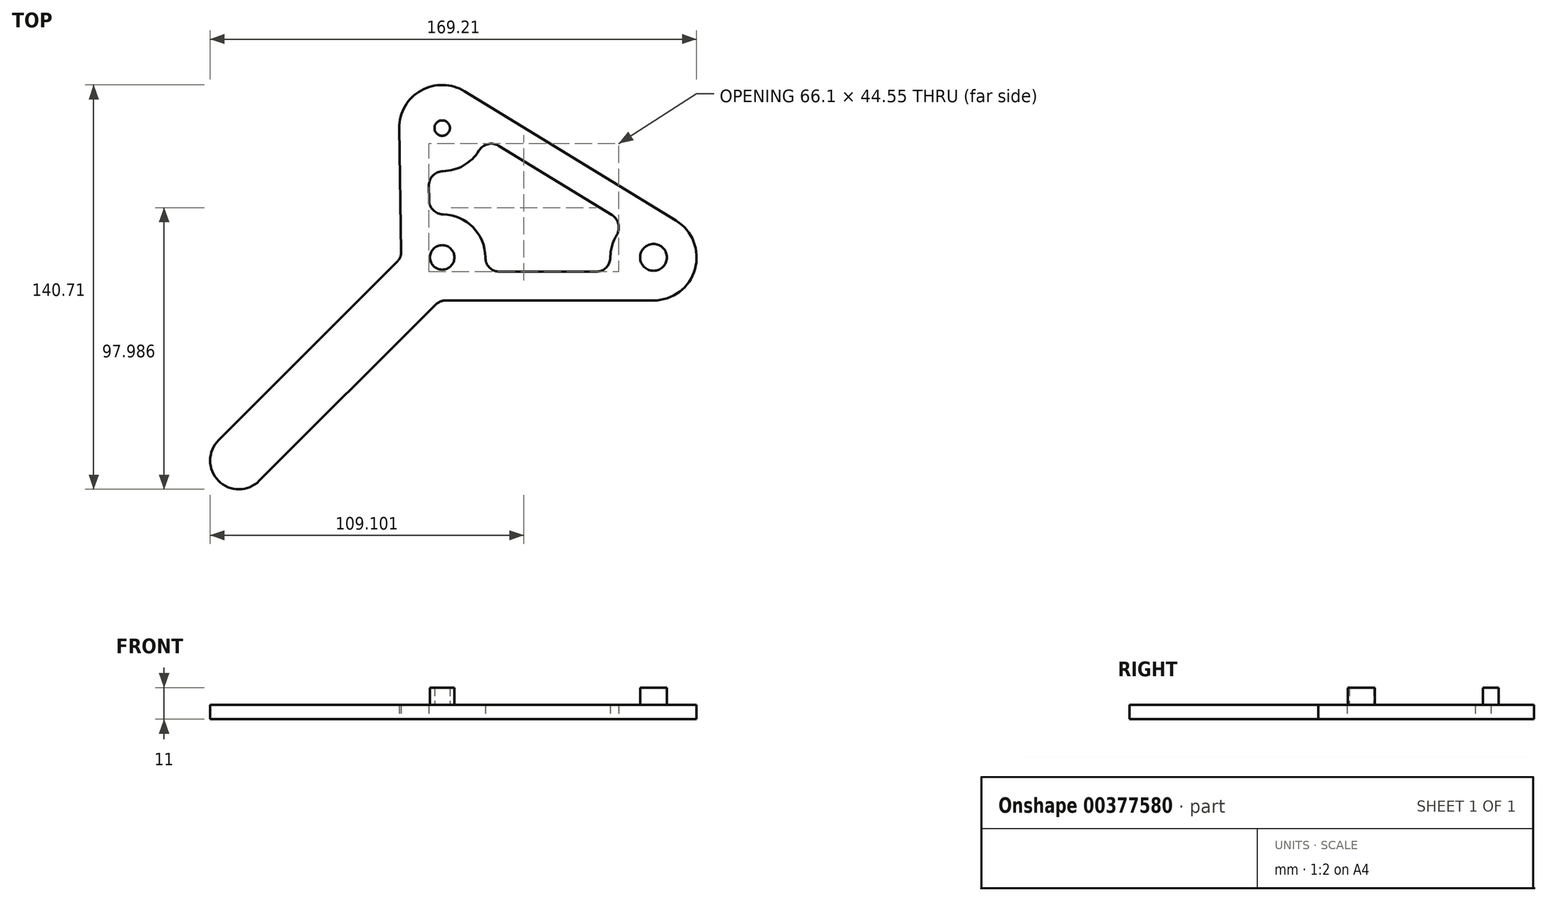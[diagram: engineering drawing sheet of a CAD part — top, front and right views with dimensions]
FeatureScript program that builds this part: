
annotation { "Feature Type Name" : "Feature", "Feature Type Description" : "" }
export const myFeature = defineFeature(function(context is Context, id is Id, definition is map)
    precondition{}
    {
        {
            var Q0;
            Q0=qCreatedBy(makeId("Top.planeOp"),FACE);
            var sketch = newSketch(context, id + "F0", { "sketchPlane" : qUnion([Q0])});
            skCircle(sketch, "E0", {"center": v(0, 45) * mm, "radius": 2.67 * mm});
            skCircle(sketch, "E1", {"center": v(0, 0) * mm, "radius": 4.26 * mm});
            skCircle(sketch, "E2", {"center": v(73.5, 0) * mm, "radius": 4.66 * mm});
            skCircle(sketch, "E3", {"center": v(0, 45) * mm, "radius": 22.5 * mm, "construction": true});
            skCircle(sketch, "E4", {"center": v(0, 0) * mm, "radius": 22.5 * mm, "construction": true});
            skCircle(sketch, "E5", {"center": v(73.5, 0) * mm, "radius": 51 * mm, "construction": true});
            skCircle(sketch, "E6", {"center": v(0, 45) * mm, "radius": 25.5 * mm, "construction": true});
            skCircle(sketch, "E7", {"center": v(0, 0) * mm, "radius": 25.5 * mm, "construction": true});
            skCircle(sketch, "E8", {"center": v(73.5, 0) * mm, "radius": 54 * mm, "construction": true});
            skLineSegment(sketch, "E9", {"start": v(0, 0) * mm, "end": v(0, 45) * mm, "construction": true});
            skLineSegment(sketch, "E10", {"start": v(0, 0) * mm, "end": v(73.5, 0) * mm, "construction": true});
            skLineSegment(sketch, "E11", {"start": v(0, 0) * mm, "end": v(-70.71, -70.71) * mm, "construction": true});
            skArc(sketch, "E12", {"start": v(0.26, 30) * mm, "mid": v(7.44, 31.98) * mm, "end": v(12.8, 37.17) * mm});
            skArc(sketch, "E13", {"start": v(60.7, 7.83) * mm, "mid": v(59.06, 4.07) * mm, "end": v(58.5, 0) * mm});
            skArc(sketch, "E14", {"start": v(15, 0) * mm, "mid": v(10.72, 10.5) * mm, "end": v(0.32, 15) * mm});
            skLineSegment(sketch, "E15", {"start": v(73.5, -15) * mm, "end": v(1.21, -15) * mm});
            skLineSegment(sketch, "E16.trimOffspring", {"start": v(7.83, 57.8) * mm, "end": v(81.33, 12.8) * mm});
            skLineSegment(sketch, "E17.trimOffspring", {"start": v(-15, 45) * mm, "end": v(-14.27, 2.03) * mm});
            skLineSegment(sketch, "E18.0", {"start": v(19.67, 38.82) * mm, "end": v(59.05, 14.7) * mm});
            skLineSegment(sketch, "E19.0", {"start": v(-4.66, 24.92) * mm, "end": v(-4.57, 19.91) * mm});
            skArc(sketch, "E20.trimOffspring", {"start": v(7.83, 57.8) * mm, "mid": v(-7.33, 58.09) * mm, "end": v(-15, 45) * mm});
            skLineSegment(sketch, "E21.trimOffspring", {"start": v(53.5, -5) * mm, "end": v(20, -5) * mm});
            skArc(sketch, "E22.trimOffspring", {"start": v(73.5, -15) * mm, "mid": v(87.94, -4.07) * mm, "end": v(81.33, 12.8) * mm});
            skLineSegment(sketch, "E23.0", {"start": v(-2.32, -16.46) * mm, "end": v(-63.64, -77.78) * mm});
            skLineSegment(sketch, "E24.0", {"start": v(-15.73, -1.6) * mm, "end": v(-77.78, -63.64) * mm});
            skArc(sketch, "E25", {"start": v(-77.78, -63.64) * mm, "mid": v(-77.78, -77.78) * mm, "end": v(-63.64, -77.78) * mm});
            skPoint(sketch, "E26.visualSharp", {"position": v(-14.23, -0.1) * mm});
            skArc(sketch, "E26.filletArc", {"start": v(-15.73, -1.6) * mm, "mid": v(-14.63, 0.07) * mm, "end": v(-14.27, 2.03) * mm});
            skPoint(sketch, "E27.visualSharp", {"position": v(-0.86, -15) * mm});
            skArc(sketch, "E27.filletArc", {"start": v(1.21, -15) * mm, "mid": v(-0.7, -15.38) * mm, "end": v(-2.32, -16.46) * mm});
            skPoint(sketch, "E28.visualSharp", {"position": v(14.67, 41.88) * mm});
            skArc(sketch, "E28.filletArc", {"start": v(19.67, 38.82) * mm, "mid": v(15.89, 39.42) * mm, "end": v(12.8, 37.17) * mm});
            skPoint(sketch, "E29.visualSharp", {"position": v(-4.76, 30.77) * mm});
            skArc(sketch, "E29.filletArc", {"start": v(0.26, 30) * mm, "mid": v(-3.25, 28.48) * mm, "end": v(-4.66, 24.92) * mm});
            skPoint(sketch, "E30.visualSharp", {"position": v(-4.48, 14.32) * mm});
            skArc(sketch, "E30.filletArc", {"start": v(-4.57, 19.91) * mm, "mid": v(-3.12, 16.47) * mm, "end": v(0.32, 15) * mm});
            skPoint(sketch, "E31.visualSharp", {"position": v(14.14, -5) * mm});
            skArc(sketch, "E31.filletArc", {"start": v(15, 0) * mm, "mid": v(16.46, -3.54) * mm, "end": v(20, -5) * mm});
            skPoint(sketch, "E32.visualSharp", {"position": v(59.36, -5) * mm});
            skArc(sketch, "E32.filletArc", {"start": v(53.5, -5) * mm, "mid": v(57.04, -3.54) * mm, "end": v(58.5, 0) * mm});
            skPoint(sketch, "E33.visualSharp", {"position": v(64.05, 11.65) * mm});
            skArc(sketch, "E33.filletArc", {"start": v(60.7, 7.83) * mm, "mid": v(61.3, 11.61) * mm, "end": v(59.05, 14.7) * mm});
            skSolve(sketch);
        }
        {
            var Q0;
            Q0=makeQuery(id+"F0.imprint","IMPRINT",FACE,{"disambiguationData":[TD([[makeQuery(id+"F0.imprint","IMPRINT",EDGE,{"derivedFrom":sQuery(id+"F0.wireOp",EDGE,"E0")}),-1.0]])]});
            extrude(context, id + "F1", {"entities" : qUnion([Q0]), "depth" : 5 * mm});
        }
        {
            var Q0;
            Q0=makeQuery(id+"F0.imprint","IMPRINT",FACE,{"disambiguationData":[TD([[makeQuery(id+"F0.imprint","IMPRINT",EDGE,{"derivedFrom":sQuery(id+"F0.wireOp",EDGE,"E0")}),1.0]])]});
            var Q1;
            Q1=makeQuery(id+"F0.imprint","IMPRINT",FACE,{"disambiguationData":[TD([[makeQuery(id+"F0.imprint","IMPRINT",EDGE,{"derivedFrom":sQuery(id+"F0.wireOp",EDGE,"E1")}),1.0]])]});
            var Q2;
            Q2=makeQuery(id+"F0.imprint","IMPRINT",FACE,{"disambiguationData":[TD([[makeQuery(id+"F0.imprint","IMPRINT",EDGE,{"derivedFrom":sQuery(id+"F0.wireOp",EDGE,"E2")}),1.0]])]});
            extrude(context, id + "F2", {"entities" : qUnion([Q0, Q1, Q2]), "operationType" : NewBodyOperationType.ADD, "depth" : 11 * mm});
        }
    });
